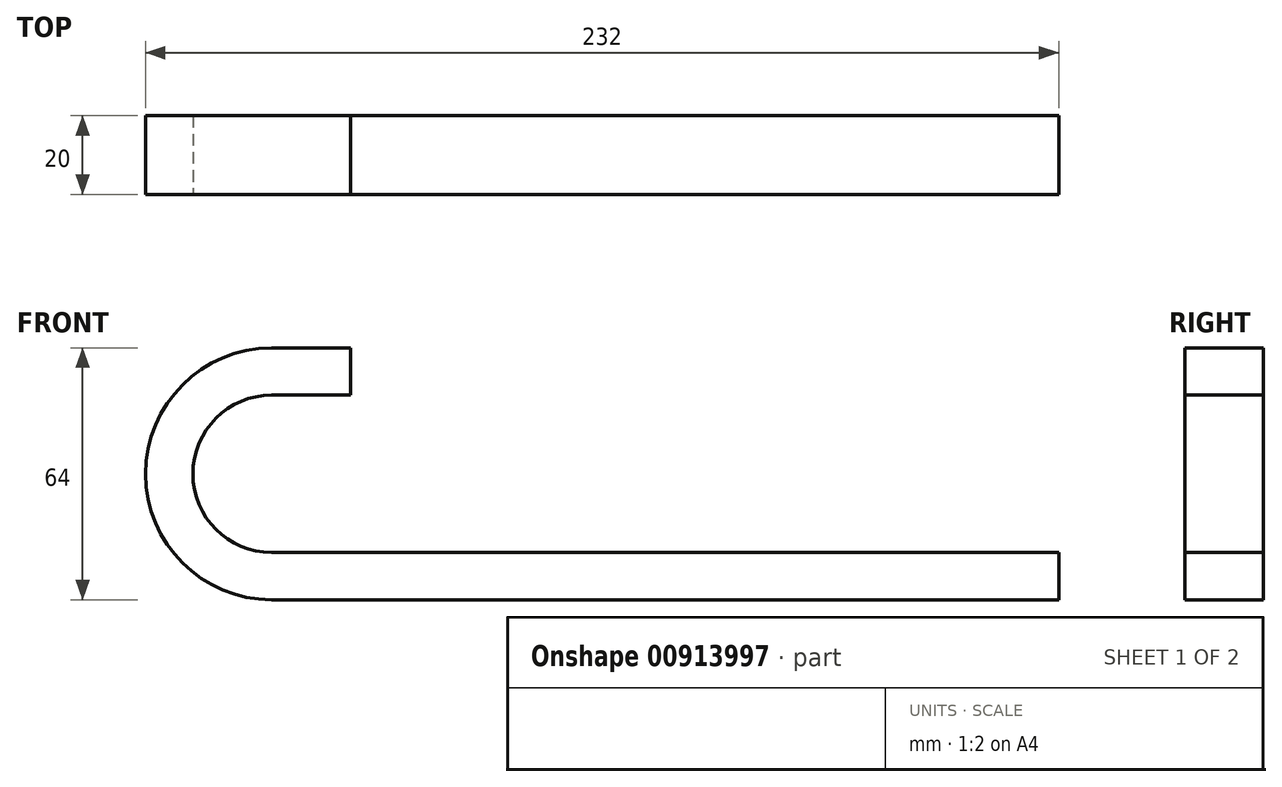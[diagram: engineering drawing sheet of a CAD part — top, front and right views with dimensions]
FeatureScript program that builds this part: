
annotation { "Feature Type Name" : "Feature", "Feature Type Description" : "" }
export const myFeature = defineFeature(function(context is Context, id is Id, definition is map)
    precondition{}
    {
        {
            var Q0;
            Q0=qCreatedBy(makeId("Front.planeOp"),FACE);
            var sketch = newSketch(context, id + "F0", { "sketchPlane" : qUnion([Q0])});
            skLineSegment(sketch, "E0", {"start": v(0, 0) * mm, "end": v(-200, 0) * mm});
            skArc(sketch, "E1", {"start": v(-200, 40) * mm, "mid": v(-220, 20) * mm, "end": v(-200, 0) * mm});
            skLineSegment(sketch, "E2", {"start": v(-200, 40) * mm, "end": v(-180, 40) * mm});
            skLineSegment(sketch, "E3", {"start": v(-180, 40) * mm, "end": v(-180, 52) * mm});
            skLineSegment(sketch, "E4", {"start": v(-180, 52) * mm, "end": v(-200, 52) * mm});
            skArc(sketch, "E5", {"start": v(-200, 52) * mm, "mid": v(-232, 20) * mm, "end": v(-200, -12) * mm});
            skLineSegment(sketch, "E6", {"start": v(-200, -12) * mm, "end": v(0, -12) * mm});
            skLineSegment(sketch, "E7", {"start": v(0, -12) * mm, "end": v(0, 0) * mm});
            skSolve(sketch);
        }
        {
            var Q0;
            Q0 = qSketchRegion(id + "F0", true);
            extrude(context, id + "F1", {"entities" : qUnion([Q0]), "oppositeDirection" : true, "depth" : 20 * mm, "offsetDistance" : 25 * mm});
        }
    });
